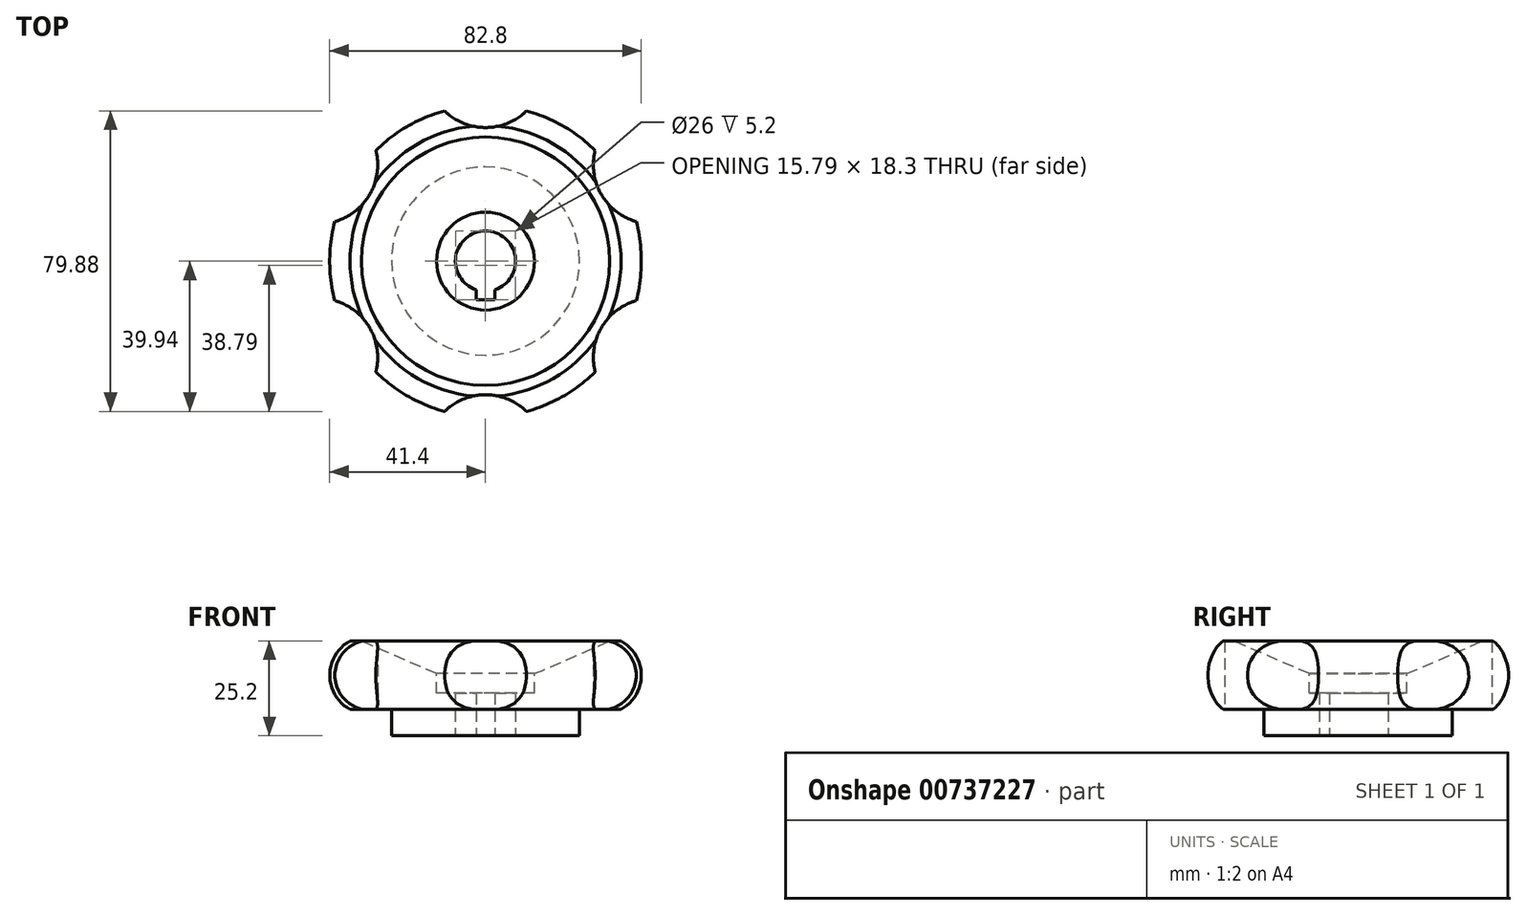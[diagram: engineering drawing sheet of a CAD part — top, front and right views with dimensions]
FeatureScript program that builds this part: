
annotation { "Feature Type Name" : "Feature", "Feature Type Description" : "" }
export const myFeature = defineFeature(function(context is Context, id is Id, definition is map)
    precondition{}
    {
        {
            var Q0;
            Q0=qCreatedBy(makeId("Front.planeOp"),FACE);
            var sketch = newSketch(context, id + "F0", { "sketchPlane" : qUnion([Q0])});
            skLineSegment(sketch, "E0", {"start": v(0, 0) * mm, "end": v(25, 0) * mm});
            skLineSegment(sketch, "E1", {"start": v(25, 0) * mm, "end": v(25, 7) * mm});
            skLineSegment(sketch, "E2", {"start": v(25, 7) * mm, "end": v(36, 7) * mm});
            skLineSegment(sketch, "E3.0", {"start": v(33, 25.2) * mm, "end": v(36, 25.2) * mm});
            skLineSegment(sketch, "E4.0", {"start": v(0, 11.3) * mm, "end": v(13, 11.3) * mm});
            skLineSegment(sketch, "E5", {"start": v(41.4, 60.5) * mm, "end": v(41.4, -63.46) * mm, "construction": true});
            skArc(sketch, "E6", {"start": v(36, 7) * mm, "mid": v(41.4, 16.1) * mm, "end": v(36, 25.2) * mm});
            skLineSegment(sketch, "E7", {"start": v(13, 11.3) * mm, "end": v(13, 16.5) * mm});
            skLineSegment(sketch, "E8", {"start": v(13, 16.5) * mm, "end": v(33, 25.2) * mm});
            skLineSegment(sketch, "E9", {"start": v(0, 11.3) * mm, "end": v(0, 0) * mm});
            skSolve(sketch);
        }
        {
            var Q0;
            Q0=makeQuery(id+"F0.imprint","IMPRINT",FACE,{"disambiguationData":[TD([[makeQuery(id+"F0.imprint","IMPRINT",EDGE,{"derivedFrom":sQuery(id+"F0.wireOp",EDGE,"E0")}),1.0]])]});
            var Q1;
            Q1=sQuery(id+"F0.wireOp",EDGE,"E9");
            revolve(context, id + "F1", {"surfaceOperationType" : NewSurfaceOperationType.NEW, "entities" : qUnion([Q0]), "axis" : qUnion([Q1]), "revolveType" : RevolveType.FULL});
        }
        {
            var Q0;
            Q0=makeQuery(id+"F1.opRevolve","SWEPT_FACE",FACE,{"disambiguationData":[OSD([sQuery(id+"F0.wireOp",EDGE,"E0")])]});
            var sketch = newSketch(context, id + "F2", { "sketchPlane" : qUnion([Q0])});
            skCircle(sketch, "E10", {"center": v(0, 0) * mm, "radius": 8 * mm});
            skLineSegment(sketch, "E11", {"start": v(-2.52, 10.3) * mm, "end": v(2.52, 10.3) * mm});
            skLineSegment(sketch, "E12", {"start": v(0, -18.1) * mm, "end": v(0, 35.5) * mm, "construction": true});
            skLineSegment(sketch, "E13", {"start": v(-2.52, 10.3) * mm, "end": v(-2.52, 7.6) * mm});
            skLineSegment(sketch, "E14.MirrorCS", {"start": v(2.52, 10.3) * mm, "end": v(2.52, 7.6) * mm});
            skPoint(sketch, "E15.orphan", {"position": v(-2.52, 3.63) * mm});
            skPoint(sketch, "E16.orphan", {"position": v(2.52, 3.63) * mm});
            skPoint(sketch, "E17.orphan", {"position": v(2.52, 11.78) * mm});
            skPoint(sketch, "E18.orphan", {"position": v(-2.52, 11.78) * mm});
            skLineSegment(sketch, "E19", {"start": v(-10.9, 48.35) * mm, "end": v(-10.9, 28.17) * mm});
            skLineSegment(sketch, "E20.MirrorCS", {"start": v(10.9, 48.35) * mm, "end": v(10.9, 28.17) * mm});
            skCircle(sketch, "E21", {"center": v(0, 0) * mm, "radius": 41.4 * mm, "construction": true});
            skCircle(sketch, "E22", {"center": v(0, 51.1) * mm, "radius": 15.6 * mm});
            skPoint(sketch, "E22.first.point", {"position": v(-10.9, 39.94) * mm});
            skPoint(sketch, "E22.first.point.positionSnap0", {"position": v(-10.9, 38.26) * mm});
            skPoint(sketch, "E22.second.point", {"position": v(10.9, 39.94) * mm});
            skCircle(sketch, "E23.1.0", {"center": v(-44.25, 25.55) * mm, "radius": 15.6 * mm});
            skCircle(sketch, "E23.2.0", {"center": v(-44.25, -25.55) * mm, "radius": 15.6 * mm});
            skCircle(sketch, "E23.3.0", {"center": v(0, -51.1) * mm, "radius": 15.6 * mm});
            skCircle(sketch, "E23.4.0", {"center": v(44.25, -25.55) * mm, "radius": 15.6 * mm});
            skCircle(sketch, "E23.5.0", {"center": v(44.25, 25.55) * mm, "radius": 15.6 * mm});
            skSolve(sketch);
        }
        {
            var Q0;
            Q0=makeQuery(id+"F2.imprint","IMPRINT",FACE,{"disambiguationData":[TD([[makeQuery(id+"F2.imprint","IMPRINT",EDGE,{"derivedFrom":sQuery(id+"F2.wireOp",EDGE,"E22")}),1.0]])]});
            var Q1;
            Q1=makeQuery(id+"F2.imprint","IMPRINT",FACE,{"disambiguationData":[TD([[makeQuery(id+"F2.imprint","IMPRINT",EDGE,{"derivedFrom":sQuery(id+"F2.wireOp",EDGE,"E23.5.0")}),1.0]])]});
            var Q2;
            Q2=makeQuery(id+"F2.imprint","IMPRINT",FACE,{"disambiguationData":[TD([[makeQuery(id+"F2.imprint","IMPRINT",EDGE,{"derivedFrom":sQuery(id+"F2.wireOp",EDGE,"E23.4.0")}),1.0]])]});
            var Q3;
            Q3=makeQuery(id+"F2.imprint","IMPRINT",FACE,{"disambiguationData":[TD([[makeQuery(id+"F2.imprint","IMPRINT",EDGE,{"derivedFrom":sQuery(id+"F2.wireOp",EDGE,"E23.3.0")}),1.0]])]});
            var Q4;
            Q4=makeQuery(id+"F2.imprint","IMPRINT",FACE,{"disambiguationData":[TD([[makeQuery(id+"F2.imprint","IMPRINT",EDGE,{"derivedFrom":sQuery(id+"F2.wireOp",EDGE,"E23.2.0")}),1.0]])]});
            var Q5;
            Q5=makeQuery(id+"F2.imprint","IMPRINT",FACE,{"disambiguationData":[TD([[makeQuery(id+"F2.imprint","IMPRINT",EDGE,{"derivedFrom":sQuery(id+"F2.wireOp",EDGE,"E23.1.0")}),1.0]])]});
            var Q6;
            {var subQ0=sQuery(id+"F2.wireOp",EDGE,"E10");var subQ1=makeQuery(id+"F2.imprint","INTERSECT",VERTEX,{"derivedFrom":[subQ0,sQuery(id+"F2.wireOp",EDGE,"E13")]});Q6=makeQuery(id+"F2.imprint","IMPRINT",FACE,{"disambiguationData":[TD([[makeQuery(id+"F2.imprint","IMPRINT",EDGE,{"disambiguationData":[TD([[subQ1,1.0]])],"derivedFrom":subQ0}),1.0]])]});}
            var Q7;
            Q7=makeQuery(id+"F2.imprint","IMPRINT",FACE,{"disambiguationData":[TD([[makeQuery(id+"F2.imprint","IMPRINT",EDGE,{"derivedFrom":sQuery(id+"F2.wireOp",EDGE,"E11")}),-1.0]])]});
            extrude(context, id + "F3", {"entities" : qUnion([Q0, Q1, Q2, Q3, Q4, Q5, Q6, Q7]), "operationType" : NewBodyOperationType.REMOVE, "endBound" : BoundingType.THROUGH_ALL, "oppositeDirection" : true, "depth" : 25 * mm, "offsetDistance" : 25 * mm});
        }
    });
